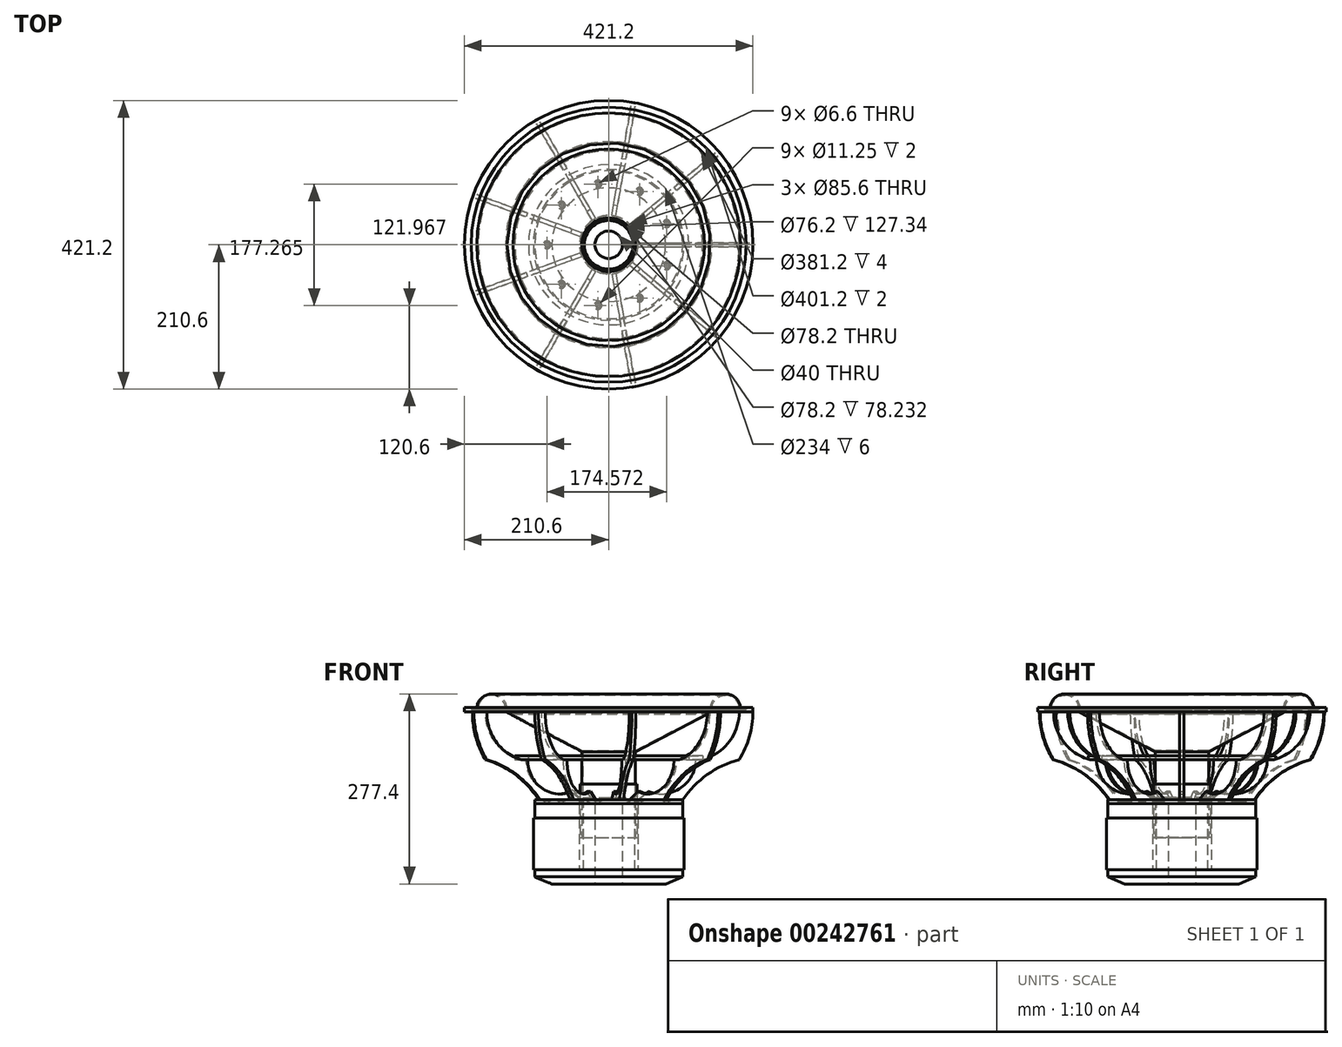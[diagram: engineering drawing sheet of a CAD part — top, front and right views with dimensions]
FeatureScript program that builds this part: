
annotation { "Feature Type Name" : "Feature", "Feature Type Description" : "" }
export const myFeature = defineFeature(function(context is Context, id is Id, definition is map)
    precondition{}
    {
        {
            var Q0;
            Q0=qCreatedBy(makeId("Front.planeOp"),FACE);
            var sketch = newSketch(context, id + "F0", { "sketchPlane" : qUnion([Q0])});
            skLineSegment(sketch, "E0.bottom", {"start": v(42.8, 0) * mm, "end": v(108, 0) * mm});
            skLineSegment(sketch, "E0.top", {"start": v(42.8, -6) * mm, "end": v(108, -6) * mm});
            skLineSegment(sketch, "E0.left", {"start": v(42.8, 0) * mm, "end": v(42.8, -6) * mm});
            skLineSegment(sketch, "E1", {"start": v(108, -6) * mm, "end": v(108, 0) * mm});
            skLineSegment(sketch, "E2", {"start": v(0, 0) * mm, "end": v(0, 32.36) * mm, "construction": true});
            skLineSegment(sketch, "E3.bottom", {"start": v(200.6, 134.34) * mm, "end": v(210.6, 134.34) * mm});
            skLineSegment(sketch, "E3.top", {"start": v(190.6, 128.34) * mm, "end": v(210.6, 128.34) * mm});
            skLineSegment(sketch, "E3.left", {"start": v(190.6, 132.34) * mm, "end": v(190.6, 128.34) * mm});
            skLineSegment(sketch, "E3.right", {"start": v(210.6, 134.34) * mm, "end": v(210.6, 128.34) * mm});
            skLineSegment(sketch, "E4", {"start": v(150.6, 128.34) * mm, "end": v(39.1, 70.03) * mm});
            skLineSegment(sketch, "E5", {"start": v(150.6, 130.03) * mm, "end": v(150.6, 128.34) * mm});
            skLineSegment(sketch, "E6", {"start": v(39.1, 71.72) * mm, "end": v(39.1, 70.03) * mm});
            skLineSegment(sketch, "E7.top", {"start": v(38.1, 71.72) * mm, "end": v(39.1, 71.72) * mm});
            skLineSegment(sketch, "E7.right", {"start": v(39.1, -55.62) * mm, "end": v(39.1, 71.72) * mm});
            skLineSegment(sketch, "E8", {"start": v(38.1, 71.72) * mm, "end": v(38.1, -55.62) * mm});
            skLineSegment(sketch, "E9", {"start": v(150.6, 130.03) * mm, "end": v(0, 130.03) * mm, "construction": true});
            skArc(sketch, "E10", {"start": v(0, 112.72) * mm, "mid": v(42.04, 108.02) * mm, "end": v(82, 94.16) * mm});
            skLineSegment(sketch, "E11", {"start": v(0, 112.72) * mm, "end": v(0, 111.72) * mm});
            skArc(sketch, "E12", {"start": v(0, 111.72) * mm, "mid": v(41.06, 106.82) * mm, "end": v(80.09, 93.16) * mm});
            skLineSegment(sketch, "E13", {"start": v(150.6, 130.03) * mm, "end": v(39.1, 71.72) * mm});
            skLineSegment(sketch, "E14", {"start": v(0, 112.72) * mm, "end": v(-8.95, 112.72) * mm, "construction": true});
            skLineSegment(sketch, "E15", {"start": v(190.6, 132.34) * mm, "end": v(200.6, 132.34) * mm});
            skLineSegment(sketch, "E16", {"start": v(200.6, 132.34) * mm, "end": v(200.6, 134.34) * mm});
            skLineSegment(sketch, "E17.right", {"start": v(110, -27) * mm, "end": v(110, -102) * mm});
            skLineSegment(sketch, "E18.top", {"start": v(108, -6) * mm, "end": v(42.8, -6) * mm});
            skLineSegment(sketch, "E18.left", {"start": v(108, -27) * mm, "end": v(108, -6) * mm});
            skLineSegment(sketch, "E18.right", {"start": v(42.8, -27) * mm, "end": v(42.8, -6) * mm});
            skLineSegment(sketch, "E19.top", {"start": v(83.05, -123) * mm, "end": v(20, -123) * mm});
            skLineSegment(sketch, "E19.left", {"start": v(108, -102) * mm, "end": v(108, -112.7) * mm});
            skLineSegment(sketch, "E19.right", {"start": v(20, -102) * mm, "end": v(20, -123) * mm});
            skLineSegment(sketch, "E20", {"start": v(108, -112.7) * mm, "end": v(83.05, -123) * mm});
            skPoint(sketch, "E21", {"position": v(42.8, -16.5) * mm});
            skLineSegment(sketch, "E22", {"start": v(139.64, 126.56) * mm, "end": v(140.57, 124.79) * mm});
            skArc(sketch, "E23", {"start": v(190.6, 132.34) * mm, "mid": v(169.38, 152.37) * mm, "end": v(150.6, 130.03) * mm});
            skLineSegment(sketch, "E24", {"start": v(200.6, 134.34) * mm, "end": v(192.5, 134.34) * mm});
            skLineSegment(sketch, "E25", {"start": v(139.64, 126.56) * mm, "end": v(148.5, 131.2) * mm});
            skArc(sketch, "E26", {"start": v(192.5, 134.34) * mm, "mid": v(168.96, 154.34) * mm, "end": v(148.5, 131.2) * mm});
            skLineSegment(sketch, "E27", {"start": v(192.5, 134.34) * mm, "end": v(190.5, 134.34) * mm, "construction": true});
            skLineSegment(sketch, "E28", {"start": v(127, 58.38) * mm, "end": v(127, 64.38) * mm});
            skLineSegment(sketch, "E29", {"start": v(117, 58.38) * mm, "end": v(42.8, 0) * mm, "construction": true});
            skLineSegment(sketch, "E30", {"start": v(150.6, 128.34) * mm, "end": v(150.6, 69.15) * mm, "construction": true});
            skCircle(sketch, "E31", {"center": v(170.53, 132.34) * mm, "radius": 20.07 * mm, "construction": true});
            skLineSegment(sketch, "E32", {"start": v(190.6, 128.34) * mm, "end": v(150.6, 69.15) * mm, "construction": true});
            skArc(sketch, "E33", {"start": v(190.46, 58.38) * mm, "mid": v(205.46, 91.94) * mm, "end": v(210.6, 128.34) * mm});
            skLineSegment(sketch, "E34.left", {"start": v(117, 58.38) * mm, "end": v(117, 64.38) * mm});
            skPoint(sketch, "E34.middle", {"position": v(127, 61.38) * mm});
            skLineSegment(sketch, "E35", {"start": v(137, 58.38) * mm, "end": v(137, 64.38) * mm});
            skLineSegment(sketch, "E36", {"start": v(137, 64.38) * mm, "end": v(117, 64.38) * mm});
            skArc(sketch, "E37", {"start": v(190.6, 128.34) * mm, "mid": v(175.66, 84.27) * mm, "end": v(137, 58.38) * mm});
            skPoint(sketch, "E38.endSnap0", {"position": v(75.4, 0) * mm});
            skLineSegment(sketch, "E39", {"start": v(42.8, 0) * mm, "end": v(58.05, 12) * mm});
            skLineSegment(sketch, "E40", {"start": v(58.05, 12) * mm, "end": v(58.05, 0) * mm});
            skArc(sketch, "E41", {"start": v(127, 58.38) * mm, "mid": v(104.88, 16.83) * mm, "end": v(58.05, 12) * mm});
            skLineSegment(sketch, "E42", {"start": v(127, 58.38) * mm, "end": v(137, 58.38) * mm});
            skLineSegment(sketch, "E43", {"start": v(127, 58.38) * mm, "end": v(117, 58.38) * mm});
            skLineSegment(sketch, "E44", {"start": v(117, 64.38) * mm, "end": v(117, 110.77) * mm, "construction": true});
            skLineSegment(sketch, "E45", {"start": v(196.55, 134.34) * mm, "end": v(196.55, 140.34) * mm});
            skLineSegment(sketch, "E46", {"start": v(196.55, 140.34) * mm, "end": v(226.55, 140.34) * mm});
            skLineSegment(sketch, "E47", {"start": v(226.55, 140.34) * mm, "end": v(226.55, 134.34) * mm});
            skLineSegment(sketch, "E48", {"start": v(226.55, 134.34) * mm, "end": v(210.6, 134.34) * mm});
            skLineSegment(sketch, "E49", {"start": v(38.1, -55.62) * mm, "end": v(41.66, -55.62) * mm});
            skLineSegment(sketch, "E50", {"start": v(41.66, -55.62) * mm, "end": v(41.66, 22.62) * mm});
            skLineSegment(sketch, "E51", {"start": v(41.66, 22.62) * mm, "end": v(39.1, 22.62) * mm});
            skLineSegment(sketch, "E52", {"start": v(42.8, -27) * mm, "end": v(42.8, -102) * mm});
            skPoint(sketch, "E53", {"position": v(41.66, -16.5) * mm});
            skLineSegment(sketch, "E54", {"start": v(42.8, -27) * mm, "end": v(110, -27) * mm});
            skLineSegment(sketch, "E55", {"start": v(20, -102) * mm, "end": v(110, -102) * mm});
            skLineSegment(sketch, "E56", {"start": v(110, -52.4) * mm, "end": v(42.8, -52.4) * mm});
            skLineSegment(sketch, "E57", {"start": v(110, -76.6) * mm, "end": v(42.8, -76.6) * mm});
            skArc(sketch, "E58", {"start": v(190.46, 58.38) * mm, "mid": v(143.97, 36.62) * mm, "end": v(108, 0) * mm});
            skLineSegment(sketch, "E59", {"start": v(39.1, -55.62) * mm, "end": v(39.1, -102) * mm, "construction": true});
            skLineSegment(sketch, "E60", {"start": v(58.05, 12) * mm, "end": v(58.05, 58.38) * mm, "construction": true});
            skLineSegment(sketch, "E61", {"start": v(20, -102) * mm, "end": v(20, -6) * mm});
            skLineSegment(sketch, "E62", {"start": v(37.5, -102) * mm, "end": v(37.5, 3.38) * mm});
            skArc(sketch, "E63", {"start": v(20, -6) * mm, "mid": v(29.06, -3.47) * mm, "end": v(35.5, 3.38) * mm});
            skLineSegment(sketch, "E64", {"start": v(20, -6) * mm, "end": v(0, -6) * mm, "construction": true});
            skLineSegment(sketch, "E65", {"start": v(35.5, 3.38) * mm, "end": v(37.5, 3.38) * mm});
            skSolve(sketch);
        }
        {
            var Q0;
            Q0=makeQuery(id+"F0.imprint","IMPRINT",FACE,{"disambiguationData":[TD([[makeQuery(id+"F0.imprint","IMPRINT",EDGE,{"derivedFrom":sQuery(id+"F0.wireOp",EDGE,"E0.bottom")}),1.0]])]});
            var Q1;
            Q1=makeQuery(id+"F0.imprint","IMPRINT",FACE,{"disambiguationData":[TD([[makeQuery(id+"F0.imprint","IMPRINT",EDGE,{"derivedFrom":sQuery(id+"F0.wireOp",EDGE,"E3.top")}),-1.0]])]});
            extrude(context, id + "F1", {"entities" : qUnion([Q0, Q1]), "depth" : 3 * mm, "hasSecondDirection" : true, "secondDirectionOppositeDirection" : true, "secondDirectionDepth" : 3 * mm});
        }
        {
            var Q0;
            Q0=makeQuery(id+"F1.opExtrude","SWEPT_BODY",BODY,{"disambiguationData":[OSD([sQuery(id+"F0.wireOp",EDGE,"E0.bottom"),sQuery(id+"F0.wireOp",EDGE,"6c7cb310-9df3-4df2-87a5-b65033ba0822.top"),sQuery(id+"F0.wireOp",EDGE,"nT3Qd54m-n4Mr-KzPj-ubfg-OKSk5NO6LqhC"),sQuery(id+"F0.wireOp",EDGE,"HfDnNz2e-wXp7-ltQI-1r98-O9Q1wdCByFx3"),sQuery(id+"F0.wireOp",EDGE,"b51f060f-5979-43c8-a97c-01c7b52eec3f")])]});
            var Q1;
            Q1=makeQuery(id+"F1.opExtrude","SWEPT_BODY",BODY,{"disambiguationData":[OSD([sQuery(id+"F0.wireOp",EDGE,"56108468-e6ef-4c31-aa1b-a381e27727b4.top"),sQuery(id+"F0.wireOp",EDGE,"E3.top"),sQuery(id+"F0.wireOp",EDGE,"4c3c0eb7-8127-4a6f-916d-201b3557d1e0"),sQuery(id+"F0.wireOp",EDGE,"e00a4080-055f-4dc8-8bab-c810e85ee1ca"),sQuery(id+"F0.wireOp",EDGE,"936a3c3a-1da7-4d78-9b4e-07095c25ca2c"),sQuery(id+"F0.wireOp",EDGE,"0a553143-d006-4ff2-9b8a-ab2828d84b0a")])]});
            var Q2;
            Q2=sQuery(id+"F0.wireOp",EDGE,"E2");
            circularPattern(context, id + "F2", {"entities" : qUnion([Q0, Q1]), "axis" : qUnion([Q2]), "angle" : 360 * degree, "instanceCount" : 9, "equalSpace" : true});
        }
        {
            var Q0;
            Q0=makeQuery(id+"F0.imprint","IMPRINT",FACE,{"disambiguationData":[TD([[makeQuery(id+"F0.imprint","IMPRINT",EDGE,{"derivedFrom":sQuery(id+"F0.wireOp",EDGE,"E0.bottom")}),-1.0]])]});
            var Q1;
            Q1=makeQuery(id+"F0.imprint","IMPRINT",FACE,{"disambiguationData":[TD([[makeQuery(id+"F0.imprint","IMPRINT",EDGE,{"derivedFrom":sQuery(id+"F0.wireOp",EDGE,"E4")}),-1.0]])]});
            var Q2;
            Q2=makeQuery(id+"F0.imprint","IMPRINT",FACE,{"disambiguationData":[TD([[makeQuery(id+"F0.imprint","IMPRINT",EDGE,{"derivedFrom":sQuery(id+"F0.wireOp",EDGE,"E3.bottom")}),-1.0]])]});
            var Q3;
            {var subQ0=sQuery(id+"F0.wireOp",EDGE,"E28");Q3=makeQuery(id+"F0.imprint","IMPRINT",FACE,{"disambiguationData":[TD([[makeQuery(id+"F0.imprint","IMPRINT",EDGE,{"derivedFrom":subQ0}),-1.0]])]});}
            var Q4;
            {var subQ0=sQuery(id+"F0.wireOp",EDGE,"E28");Q4=makeQuery(id+"F0.imprint","IMPRINT",FACE,{"disambiguationData":[TD([[makeQuery(id+"F0.imprint","IMPRINT",EDGE,{"derivedFrom":subQ0}),1.0]])]});}
            var Q5;
            {var subQ6=sQuery(id+"F0.wireOp",EDGE,"E56");Q5=makeQuery(id+"F0.imprint","IMPRINT",FACE,{"disambiguationData":[TD([[makeQuery(id+"F0.imprint","IMPRINT",EDGE,{"derivedFrom":subQ6}),-1.0]])]});}
            var Q6;
            {var subQ0=sQuery(id+"F0.wireOp",EDGE,"E56");Q6=makeQuery(id+"F0.imprint","IMPRINT",FACE,{"disambiguationData":[TD([[makeQuery(id+"F0.imprint","IMPRINT",EDGE,{"derivedFrom":subQ0}),1.0]])]});}
            var Q7;
            {var subQ6=sQuery(id+"F0.wireOp",EDGE,"E57");Q7=makeQuery(id+"F0.imprint","IMPRINT",FACE,{"disambiguationData":[TD([[makeQuery(id+"F0.imprint","IMPRINT",EDGE,{"derivedFrom":subQ6}),1.0]])]});}
            var Q8;
            {var subQ4=sQuery(id+"F0.wireOp",EDGE,"E50");Q8=makeQuery(id+"F0.imprint","IMPRINT",FACE,{"disambiguationData":[TD([[makeQuery(id+"F0.imprint","IMPRINT",EDGE,{"derivedFrom":subQ4}),1.0]])]});}
            var Q9;
            Q9=sQuery(id+"F0.wireOp",EDGE,"E2");
            revolve(context, id + "F3", {"entities" : qUnion([Q0, Q1, Q2, Q3, Q4, Q5, Q6, Q7, Q8]), "axis" : qUnion([Q9]), "revolveType" : RevolveType.FULL});
        }
        {
            var Q0;
            {var subQ5=sQuery(id+"F0.wireOp",EDGE,"E7.top");Q0=makeQuery(id+"F0.imprint","IMPRINT",FACE,{"disambiguationData":[TD([[makeQuery(id+"F0.imprint","IMPRINT",EDGE,{"derivedFrom":subQ5}),-1.0]])]});}
            var Q1;
            {var subQ0=sQuery(id+"F0.wireOp",EDGE,"E10");Q1=makeQuery(id+"F0.imprint","IMPRINT",FACE,{"disambiguationData":[TD([[makeQuery(id+"F0.imprint","IMPRINT",EDGE,{"derivedFrom":subQ0}),-1.0]])]});}
            var Q2;
            {var subQ3=sQuery(id+"F0.wireOp",EDGE,"E18.left");Q2=makeQuery(id+"F0.imprint","IMPRINT",FACE,{"disambiguationData":[TD([[makeQuery(id+"F0.imprint","IMPRINT",EDGE,{"derivedFrom":subQ3}),1.0]])]});}
            var Q3;
            Q3=makeQuery(id+"F0.imprint","IMPRINT",FACE,{"disambiguationData":[TD([[makeQuery(id+"F0.imprint","IMPRINT",EDGE,{"derivedFrom":sQuery(id+"F0.wireOp",EDGE,"E19.top")}),-1.0]])]});
            var Q4;
            Q4=makeQuery(id+"F0.imprint","IMPRINT",FACE,{"disambiguationData":[TD([[makeQuery(id+"F0.imprint","IMPRINT",EDGE,{"derivedFrom":sQuery(id+"F0.wireOp",EDGE,"E15")}),1.0]])]});
            var Q5;
            {var subQ1=sQuery(id+"F0.wireOp",EDGE,"E61");Q5=makeQuery(id+"F0.imprint","IMPRINT",FACE,{"disambiguationData":[TD([[makeQuery(id+"F0.imprint","IMPRINT",EDGE,{"derivedFrom":subQ1}),-1.0]])]});}
            var Q6;
            Q6=sQuery(id+"F0.wireOp",EDGE,"E2");
            revolve(context, id + "F4", {"entities" : qUnion([Q0, Q1, Q2, Q3, Q4, Q5]), "axis" : qUnion([Q6]), "revolveType" : RevolveType.FULL});
        }
        {
            var Q0;
            Q0=makeQuery(id+"F3.opRevolve","SWEPT_FACE",FACE,{"disambiguationData":[OSD([sQuery(id+"F0.wireOp",EDGE,"E0.bottom")])]});
            var sketch = newSketch(context, id + "F5", { "sketchPlane" : qUnion([Q0])});
            skPoint(sketch, "E66", {"position": v(-90, 0) * mm});
            skPoint(sketch, "E67.1.0", {"position": v(-68.94, -57.85) * mm});
            skPoint(sketch, "E67.2.0", {"position": v(-15.63, -88.63) * mm});
            skPoint(sketch, "E67.3.0", {"position": v(45, -77.94) * mm});
            skPoint(sketch, "E67.4.0", {"position": v(84.57, -30.78) * mm});
            skPoint(sketch, "E67.center", {"position": v(0, 0) * mm});
            skPoint(sketch, "E68.0.5.0", {"position": v(84.57, 30.78) * mm});
            skPoint(sketch, "E69.0.6.0", {"position": v(45, 77.94) * mm});
            skPoint(sketch, "E69.0.7.0", {"position": v(-15.63, 88.63) * mm});
            skPoint(sketch, "E69.0.8.0", {"position": v(-68.94, 57.85) * mm});
            skSolve(sketch);
        }
        {
            var Q0;
            Q0=sQuery(id+"F5.wireOp",VERTEX,"E66");
            var Q1;
            Q1=sQuery(id+"F5.wireOp",VERTEX,"E67.4.0");
            var Q2;
            Q2=sQuery(id+"F5.wireOp",VERTEX,"E67.3.0");
            var Q3;
            Q3=sQuery(id+"F5.wireOp",VERTEX,"E67.2.0");
            var Q4;
            Q4=sQuery(id+"F5.wireOp",VERTEX,"E67.1.0");
            var Q5;
            Q5=sQuery(id+"F5.wireOp",VERTEX,"E68.0.5.0");
            var Q6;
            Q6=sQuery(id+"F5.wireOp",VERTEX,"E69.0.7.0");
            var Q7;
            Q7=sQuery(id+"F5.wireOp",VERTEX,"E69.0.8.0");
            var Q8;
            Q8=sQuery(id+"F5.wireOp",VERTEX,"E69.0.6.0");
            var Q9;
            Q9=makeQuery(id+"F3.opRevolve","SWEPT_BODY",BODY,{"disambiguationData":[OSD([sQuery(id+"F0.wireOp",EDGE,"E0.bottom"),sQuery(id+"F0.wireOp",EDGE,"E0.left"),sQuery(id+"F0.wireOp",EDGE,"E1"),sQuery(id+"F0.wireOp",EDGE,"E18.top")])]});
            hole(context, id + "F6", {"style" : HoleStyle.C_BORE, "endStyle" : HoleEndStyle.THROUGH, "holeDiameter" : 6.6 * mm, "cBoreDiameter" : 11.25 * mm, "cBoreDepth" : 2 * mm, "locations" : qUnion([Q0, Q1, Q2, Q3, Q4, Q5, Q6, Q7, Q8]), "scope" : qUnion([Q9]), "tappedDepth" : 12 * mm, "tapClearance" : 3});
        }
    });
